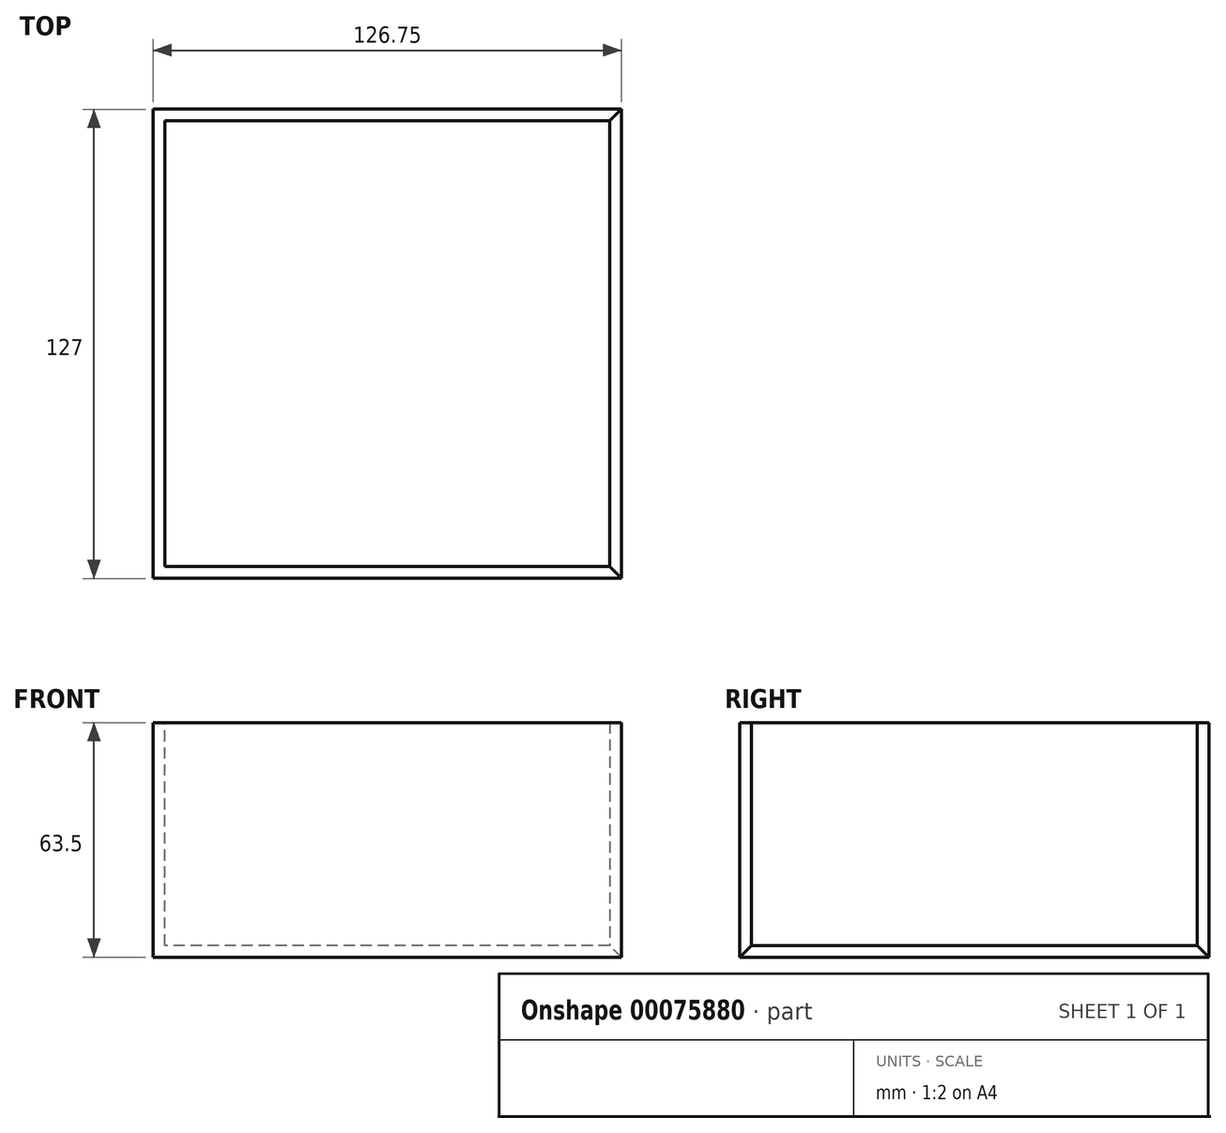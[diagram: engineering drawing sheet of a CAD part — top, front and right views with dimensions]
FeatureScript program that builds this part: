
annotation { "Feature Type Name" : "Feature", "Feature Type Description" : "" }
export const myFeature = defineFeature(function(context is Context, id is Id, definition is map)
    precondition{}
    {
        {
            var Q0;
            Q0=qCreatedBy(makeId("Top.planeOp"),FACE);
            var sketch = newSketch(context, id + "F0", { "sketchPlane" : qUnion([Q0])});
            skLineSegment(sketch, "E0.bottom", {"start": v(-53.66, 66.92) * mm, "end": v(73.34, 66.92) * mm});
            skLineSegment(sketch, "E0.top", {"start": v(-53.66, -60.08) * mm, "end": v(73.34, -60.08) * mm});
            skLineSegment(sketch, "E0.left", {"start": v(-53.66, 66.92) * mm, "end": v(-53.66, -60.08) * mm});
            skLineSegment(sketch, "E0.right", {"start": v(73.34, 66.92) * mm, "end": v(73.34, -60.08) * mm});
            skSolve(sketch);
        }
        {
            var Q0;
            Q0 = qSketchRegion(id + "F0", true);
            extrude(context, id + "F1", {"entities" : qUnion([Q0]), "depth" : 63.5 * mm});
        }
        {
            var Q0;
            Q0=makeQuery(id+"F1.opExtrude","CAP_FACE",FACE,{"disambiguationData":[OSD([sQuery(id+"F0.wireOp",EDGE,"E0.bottom"),sQuery(id+"F0.wireOp",EDGE,"E0.top"),sQuery(id+"F0.wireOp",EDGE,"E0.left"),sQuery(id+"F0.wireOp",EDGE,"E0.right")])],"isStart":false});
            var sketch = newSketch(context, id + "F2", { "sketchPlane" : qUnion([Q0])});
            skLineSegment(sketch, "E1.bottom", {"start": v(70.17, -56.9) * mm, "end": v(-50.48, -56.9) * mm});
            skLineSegment(sketch, "E1.top", {"start": v(70.17, 63.75) * mm, "end": v(-50.48, 63.75) * mm});
            skLineSegment(sketch, "E1.left", {"start": v(70.17, -56.9) * mm, "end": v(70.17, 63.75) * mm});
            skLineSegment(sketch, "E1.right", {"start": v(-50.48, -56.9) * mm, "end": v(-50.48, 63.75) * mm});
            skPoint(sketch, "E1.middle", {"position": v(9.84, 3.42) * mm});
            skPoint(sketch, "E1.middle.positionSnap0", {"position": v(-53.66, 3.42) * mm});
            skPoint(sketch, "E1.middle.positionSnap1", {"position": v(9.84, 66.92) * mm});
            skPoint(sketch, "E1.centerSnap0", {"position": v(-53.66, 3.42) * mm});
            skPoint(sketch, "E1.centerSnap1", {"position": v(9.84, 66.92) * mm});
            skLineSegment(sketch, "E2.bottom", {"start": v(70.17, 63.75) * mm, "end": v(110.33, 63.75) * mm});
            skLineSegment(sketch, "E2.top", {"start": v(70.17, -56.9) * mm, "end": v(110.33, -56.9) * mm});
            skLineSegment(sketch, "E2.left", {"start": v(70.17, 63.75) * mm, "end": v(70.17, -56.9) * mm});
            skLineSegment(sketch, "E2.right", {"start": v(110.33, 63.75) * mm, "end": v(110.33, -56.9) * mm});
            skSolve(sketch);
        }
        {
            var Q0;
            Q0 = qSketchRegion(id + "F2", true);
            extrude(context, id + "F3", {"entities" : qUnion([Q0]), "operationType" : NewBodyOperationType.REMOVE, "oppositeDirection" : true, "depth" : 60.32 * mm});
        }
        {
            var Q0;
            Q0=makeQuery(id+"F3.boolean.opBoolean","INTERSECT",EDGE,{"derivedFrom":[makeQuery(id+"F1.opExtrude","SWEPT_FACE",FACE,{"disambiguationData":[OSD([sQuery(id+"F0.wireOp",EDGE,"E0.right")])]}),makeQuery(id+"F3.opExtrude","SWEPT_FACE",FACE,{"disambiguationData":[OSD([sQuery(id+"F2.wireOp",EDGE,"E1.bottom"),sQuery(id+"F2.wireOp",EDGE,"E2.top")])]})]});
            var Q1;
            Q1=makeQuery(id+"F3.boolean.opBoolean","INTERSECT",EDGE,{"derivedFrom":[makeQuery(id+"F1.opExtrude","SWEPT_FACE",FACE,{"disambiguationData":[OSD([sQuery(id+"F0.wireOp",EDGE,"E0.right")])]}),makeQuery(id+"F3.opExtrude","CAP_FACE",FACE,{"disambiguationData":[OSD([sQuery(id+"F2.wireOp",EDGE,"E1.bottom"),sQuery(id+"F2.wireOp",EDGE,"E1.top"),sQuery(id+"F2.wireOp",EDGE,"E1.right"),sQuery(id+"F2.wireOp",EDGE,"E2.bottom"),sQuery(id+"F2.wireOp",EDGE,"E2.top"),sQuery(id+"F2.wireOp",EDGE,"E2.right")])],"isStart":false})]});
            var Q2;
            Q2=makeQuery(id+"F3.boolean.opBoolean","INTERSECT",EDGE,{"derivedFrom":[makeQuery(id+"F1.opExtrude","SWEPT_FACE",FACE,{"disambiguationData":[OSD([sQuery(id+"F0.wireOp",EDGE,"E0.right")])]}),makeQuery(id+"F3.opExtrude","SWEPT_FACE",FACE,{"disambiguationData":[OSD([sQuery(id+"F2.wireOp",EDGE,"E1.top"),sQuery(id+"F2.wireOp",EDGE,"E2.bottom")])]})]});
            chamfer(context, id + "F4", {"entities" : qUnion([Q0, Q1, Q2]), "width" : 3.43 * mm, "tangentPropagation" : true});
        }
    });
